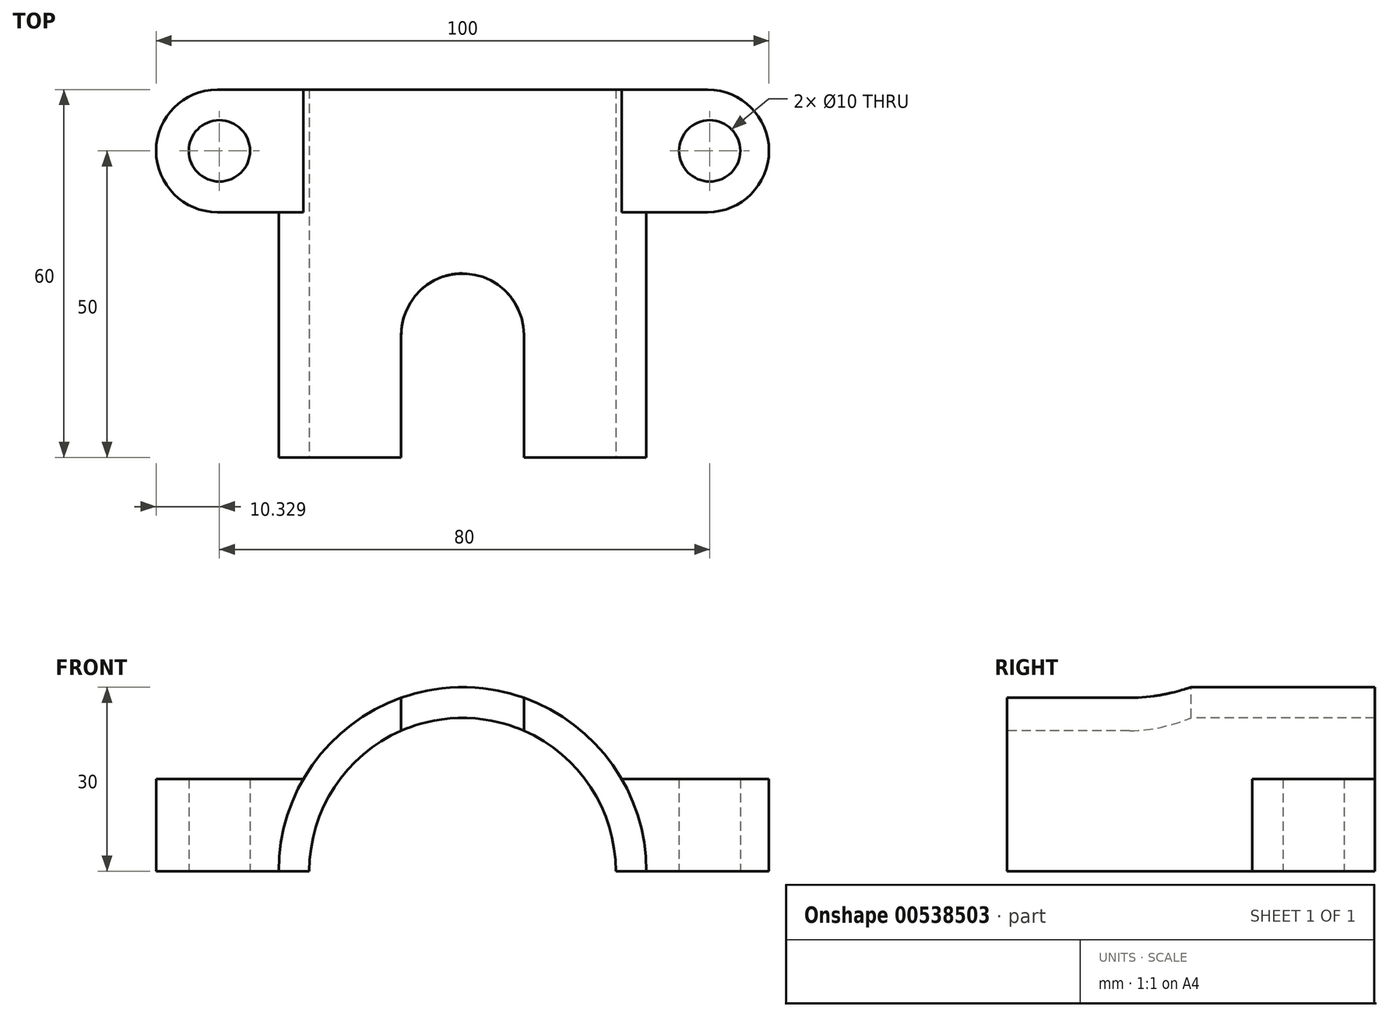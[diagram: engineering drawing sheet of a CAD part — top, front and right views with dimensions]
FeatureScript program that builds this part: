
annotation { "Feature Type Name" : "Feature", "Feature Type Description" : "" }
export const myFeature = defineFeature(function(context is Context, id is Id, definition is map)
    precondition{}
    {
        {
            var Q0;
            Q0=qCreatedBy(makeId("Front.planeOp"),FACE);
            var sketch = newSketch(context, id + "F0", { "sketchPlane" : qUnion([Q0])});
            skCircle(sketch, "E0", {"center": v(0, 0) * mm, "radius": 30 * mm});
            skSolve(sketch);
        }
        {
            var Q0;
            Q0=qSketchRegion(id+"F0",true);
            extrude(context, id + "F1", {"entities" : qUnion([Q0]), "depth" : 60 * mm, "offsetDistance" : 25 * mm});
        }
        {
            var Q0;
            Q0=makeQuery(id+"F1.opExtrude","CAP_FACE",FACE,{"disambiguationData":[OSD([sQuery(id+"F0.wireOp",EDGE,"E0")])],"isStart":false});
            var sketch = newSketch(context, id + "F2", { "sketchPlane" : qUnion([Q0])});
            skLineSegment(sketch, "E1", {"start": v(-30, 0) * mm, "end": v(30, 0) * mm});
            skSolve(sketch);
        }
        {
            var Q0;
            {var subQ0=sQuery(id+"F2.wireOp",EDGE,"E1");Q0=makeQuery(id+"F2.imprint","IMPRINT",FACE,{"disambiguationData":[TD([[makeQuery(id+"F2.imprint","IMPRINT",EDGE,{"derivedFrom":subQ0}),-1.0]])]});}
            extrude(context, id + "F3", {"entities" : qUnion([Q0]), "operationType" : NewBodyOperationType.REMOVE, "endBound" : BoundingType.UP_TO_NEXT, "oppositeDirection" : true, "depth" : 25 * mm, "offsetDistance" : 25 * mm});
        }
        {
            var Q0;
            Q0=qCreatedBy(makeId("Top.planeOp"),FACE);
            var sketch = newSketch(context, id + "F4", { "sketchPlane" : qUnion([Q0])});
            skLineSegment(sketch, "E2", {"start": v(-40, 0) * mm, "end": v(40, 0) * mm});
            skLineSegment(sketch, "E3", {"start": v(-39.67, -10) * mm, "end": v(40.33, -10) * mm, "construction": true});
            skLineSegment(sketch, "E4", {"start": v(-40, -20) * mm, "end": v(40, -20) * mm});
            skArc(sketch, "E5", {"start": v(40, -20) * mm, "mid": v(50, -10) * mm, "end": v(40, 0) * mm});
            skArc(sketch, "E6", {"start": v(-40, 0) * mm, "mid": v(-50, -10) * mm, "end": v(-40, -20) * mm});
            skCircle(sketch, "E7", {"center": v(-39.67, -10) * mm, "radius": 5 * mm});
            skCircle(sketch, "E8", {"center": v(40.33, -10) * mm, "radius": 5 * mm});
            skSolve(sketch);
        }
        {
            var Q0;
            Q0=makeQuery(id+"F4.imprint","IMPRINT",FACE,{"disambiguationData":[TD([[makeQuery(id+"F4.imprint","IMPRINT",EDGE,{"derivedFrom":sQuery(id+"F4.wireOp",EDGE,"E2")}),-1.0]])]});
            extrude(context, id + "F5", {"entities" : qUnion([Q0]), "operationType" : NewBodyOperationType.ADD, "depth" : 15 * mm, "offsetDistance" : 25 * mm});
        }
        {
            var Q0;
            Q0=makeQuery(id+"F1.opExtrude","CAP_FACE",FACE,{"disambiguationData":[OSD([sQuery(id+"F0.wireOp",EDGE,"E0")])],"isStart":false});
            var sketch = newSketch(context, id + "F6", { "sketchPlane" : qUnion([Q0])});
            skCircle(sketch, "E9", {"center": v(0, 0) * mm, "radius": 25 * mm});
            skSolve(sketch);
        }
        {
            var Q0;
            {var subQ0=sQuery(id+"F6.wireOp",EDGE,"E9");var subQ1=makeQuery(id+"F3.boolean.opBoolean","COPY",EDGE,{"derivedFrom":makeQuery(id+"F3.opExtrude","CAP_EDGE",EDGE,{"disambiguationData":[OSD([sQuery(id+"F2.wireOp",EDGE,"E1")])],"isStart":true})});var subQ2=makeQuery(id+"F6.imprint","INTERSECT",VERTEX,{"disambiguationData":[OD(0.0)],"derivedFrom":[subQ1,subQ0]});Q0=makeQuery(id+"F6.imprint","IMPRINT",FACE,{"disambiguationData":[TD([[makeQuery(id+"F6.imprint","IMPRINT",EDGE,{"disambiguationData":[TD([[subQ2,1.0]])],"derivedFrom":subQ0}),1.0]])]});}
            extrude(context, id + "F7", {"entities" : qUnion([Q0]), "operationType" : NewBodyOperationType.REMOVE, "endBound" : BoundingType.UP_TO_NEXT, "oppositeDirection" : true, "depth" : 25 * mm, "offsetDistance" : 25 * mm});
        }
        {
            var Q0;
            Q0=makeQuery(id+"F1.opExtrude","CAP_EDGE",EDGE,{"disambiguationData":[OSD([sQuery(id+"F0.wireOp",EDGE,"E0")])],"isStart":false});
            cPoint(context, id + "F8", {"entities" : qUnion([Q0]), "parameter" : 0.5});
        }
        {
            var Q0;
            Q0=qCreatedBy(makeId("Top.planeOp"),FACE);
            var Q1;
            Q1=qCreatedBy(id+"F8",VERTEX);
            cPlane(context, id + "F9", {"entities" : qUnion([Q0, Q1]), "cplaneType" : CPlaneType.PLANE_POINT, "offset" : 25 * mm, "width" : 150 * mm, "height" : 150 * mm});
        }
        {
            var Q0;
            Q0=qCreatedBy(id+"F9.planeOp",FACE);
            var sketch = newSketch(context, id + "F10", { "sketchPlane" : qUnion([Q0])});
            skLineSegment(sketch, "E10.bottom", {"start": v(10, -40) * mm, "end": v(-10, -40) * mm});
            skLineSegment(sketch, "E10.top", {"start": v(10, -80) * mm, "end": v(-10, -80) * mm});
            skLineSegment(sketch, "E10.left", {"start": v(10, -40) * mm, "end": v(10, -80) * mm});
            skLineSegment(sketch, "E10.right", {"start": v(-10, -40) * mm, "end": v(-10, -80) * mm});
            skPoint(sketch, "E10.middle", {"position": v(0, -60) * mm});
            skArc(sketch, "E11", {"start": v(10, -40) * mm, "mid": v(0, -30) * mm, "end": v(-10, -40) * mm});
            skSolve(sketch);
        }
        {
            var Q0;
            Q0=makeQuery(id+"F10.imprint","IMPRINT",FACE,{"disambiguationData":[TD([[makeQuery(id+"F10.imprint","IMPRINT",EDGE,{"derivedFrom":sQuery(id+"F10.wireOp",EDGE,"E10.bottom")}),-1.0]])]});
            var Q1;
            Q1=makeQuery(id+"F10.imprint","IMPRINT",FACE,{"disambiguationData":[TD([[makeQuery(id+"F10.imprint","IMPRINT",EDGE,{"derivedFrom":sQuery(id+"F10.wireOp",EDGE,"E10.bottom")}),1.0]])]});
            extrude(context, id + "F11", {"entities" : qUnion([Q0, Q1]), "operationType" : NewBodyOperationType.REMOVE, "oppositeDirection" : true, "depth" : 25 * mm, "offsetDistance" : 25 * mm});
        }
    });
